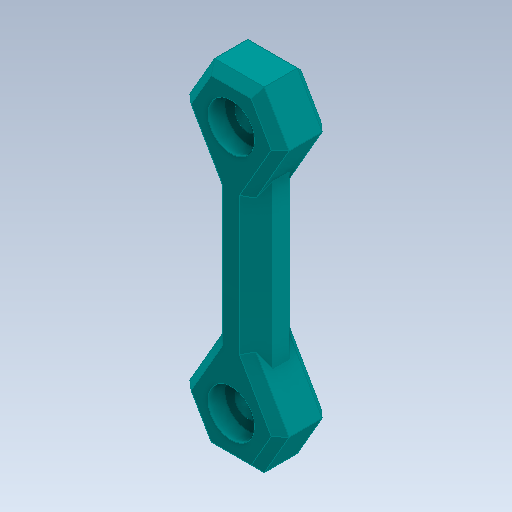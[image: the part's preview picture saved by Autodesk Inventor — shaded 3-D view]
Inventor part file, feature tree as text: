
AUTODESK INVENTOR PART (.ipt)
format: ipt  version: 2020 (Build 240168000, 168)  size: 196,608 bytes
history: native  units: in
note: dims shown in document units (in); Inventor stores cm internally (conversion verified against a paired STEP export)
features: extrude x2, chamfer x2, sketch x2, mirror x1, projected_geometry x1
ambient origin geometry x8: Origin, YZ Plane, XZ Plane, XY Plane, X Axis, Y Axis, Z Axis, Center Point
bodies: Solid1 (feature_tree)
feature tree (8):
  extrude  "Extrusion1"  Depth=0.2362in
  extrude  "Extrusion2"  Depth=0.0787in
  chamfer  "Chamfer1"  Distance=0.2362in
  chamfer  "Chamfer2"  Distance=1.1811in
  mirror  "Mirror1"
  sketch  "Sketch1"  dims[d0=0.122in d1=0.2362in]
  sketch  "Sketch2"  dims[d2=1.1811in d3=0.122in d4=0.2362in d5=1.1811in d6=0.1181in d7=0.2362in d8=0.2362in d9=0.1181in d10=0.0in d11=0.2205in d12=0.2205in d13=0.0787in d14=0.0in d15=0.0787in d16=0.0787in d17=45.0deg d18=0.0394in d19=0.0787in d20=45.0deg]
  projected_geometry  "Projected Loop1"
